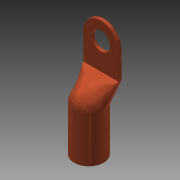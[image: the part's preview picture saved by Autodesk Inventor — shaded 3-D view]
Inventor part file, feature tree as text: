
AUTODESK INVENTOR PART (.ipt)
format: ipt  version: 2014 (Build 180170000, 170)  size: 398,848 bytes
history: native  units: in
note: dims shown in document units (in); Inventor stores cm internally (conversion verified against a paired STEP export)
features: sketch x6, fillet x5, extrude x3, other x3, plane x2, revolve x2, projected_geometry x2, split x1, loft x1, chamfer x1
ambient origin geometry x8: Origin, YZ Plane, XZ Plane, XY Plane, X Axis, Y Axis, Z Axis, Center Point
bodies: Solid1 (feature_tree)
feature tree (26):
  extrude  "Extrusion1"  Depth=0.75in
  plane  "Work Plane1"
  sketch  "Sketch2"  dims[d2=0.0625in d3=0.0in d4=0.125in]
  plane  "Work Plane2"
  revolve  "Revolution1"  [1 undecoded]
  split  "Split1"
  loft  "Loft1"
  fillet  "Fillet5"  Radius=0.5625in
  fillet  "Fillet6"  [1 undecoded]
  fillet  "Fillet7"  [1 undecoded]
  fillet  "Fillet8"  Radius=0.75in
  fillet  "Fillet9"  Radius=0.15in
  extrude  "Extrusion2"  Depth=0.25in
  revolve  "Revolution2"  [1 undecoded]
  chamfer  "Chamfer2"  Distance=0.875in
  sketch  "Sketch1"  dims[d0=0.375in d1=0.75in]
  sketch  "Sketch3"  dims[d5=0.625in d6=90.0deg d7=0.5625in d8=0.0in d9=0.0in d10=90.0deg d11=0.0in d12=90.0deg d17=0.75in d18=0.15in]
  sketch  "Sketch4"  dims[d22=0.01in d23=0.25in]
  other  "Srf1"
  other  "Edges1"
  other  "Edges2"
  sketch  "Sketch6"  dims[d24=0.25in d25=0.0625in d26=0.875in d27=0.0in]
  projected_geometry  "Projected Loop1"
  sketch  "Sketch7"  dims[d28=90.0deg d29=0.005in d30=0.125in d31=45.0deg]
  projected_geometry  "Projected Loop2"
  extrude  "ExtrusionSrf1"  Depth=0.005in TaperAngle=45.0deg
note: 4 required parameter values undecoded (feature->parameter linkage not recoverable at this tier; creation-order binding heuristic only, values carry confidence <= 0.55)